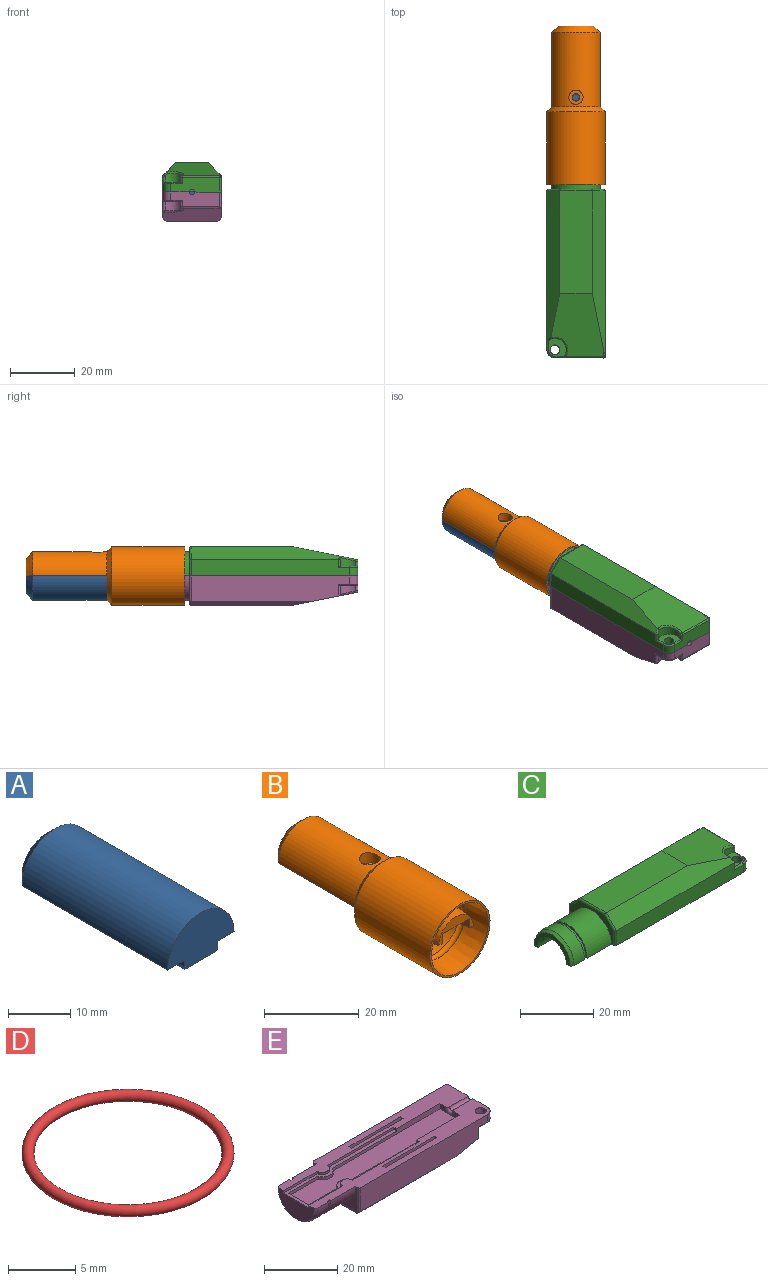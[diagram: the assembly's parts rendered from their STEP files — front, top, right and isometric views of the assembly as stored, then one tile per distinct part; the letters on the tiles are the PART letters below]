
ASSEMBLY  parts=5 mates=4
PART A: 19 faces, bbox 15x35x9.3 mm
  f0: plane 11x5.5mm, normal (0,1,0), area 43mm2, adj f1,f4,f13
  f1: plane 35x15mm, normal (0,0,-1), area 426.5mm2, adj f0,f2,f3,f4,f5,f6,f7,f8
  f2: cylinder r=7.5mm len=33mm, axis (0,1,0), area 777.5mm2, adj f1,f3,f13
  f3: plane 15x9.3mm, normal (0,-1,0), area 101.9mm2, adj f1,f2,f5,f6,f12,f17,f18
  f4: cylinder r=1.7mm len=17mm, axis (0,1,0), area 85mm2, adj f0,f1,f14
  f5: plane 11x1.2mm, normal (1,0,0), area 13.2mm2, adj f1,f3,f11,f18
  f6: plane 11x1.2mm, normal (-1,0,0), area 13.2mm2, adj f1,f3,f7,f17
  f7: plane 1.8x1mm, normal (0,1,0), area 1.7mm2, adj f1,f6,f8,f12,f17
  f8: plane 9x1.8mm, normal (1,0,0), area 16.2mm2, adj f1,f7,f9,f12
  f9: plane 5.6x1.8mm, normal (0,1,0), area 10.1mm2, adj f1,f8,f10,f12
  f10: plane 9x1.8mm, normal (-1,0,0), area 16.2mm2, adj f1,f9,f11,f12
  f11: plane 1.8x1mm, normal (0,1,0), area 1.7mm2, adj f1,f5,f10,f12,f18
  f12: plane 11x7.2mm, normal (0,0,-1), area 28.8mm2, adj f3,f7,f8,f9,f10,f11,f17,f18
  f13: cone r=7.5mm half-angle=45deg, axis (0,-1,0), area 57.8mm2, adj f0,f1,f2
  f14: plane 3.4x1.7mm, normal (0,0.71,-0.71), area 6.4mm2, adj f1,f4
  f15: cylinder r=1.05mm len=6mm, axis (0,0,-1), area 39.6mm2, adj f1,f16
  f16: plane 2.1x2.1mm, normal (0,0,-1), area 3.5mm2, adj f15
  f17: plane 11x0.6mm, normal (-0.95,0,-0.32), area 7mm2, adj f3,f6,f7,f12
  f18: plane 11x0.6mm, normal (0.95,0,-0.32), area 7mm2, adj f3,f5,f11,f12
PART B: 29 faces, bbox 18x48.9x18 mm
  f0: plane 15.6x15.6mm, normal (0,-1,0), area 52.9mm2, adj f4,f7,f8,f21,f28
  f1: cone r=9mm half-angle=45deg, axis (0,-1,0), area 106.6mm2, adj f3,f4,f7,f20,f28
  f2: cylinder r=1.7mm len=12.6mm, axis (0,1,0), area 66.5mm2, adj f4,f5,f7,f11,f25
  f3: cylinder r=7.5mm len=22.9mm, axis (0,1,0), area 524.2mm2, adj f1,f4,f7,f13,f15
  f4: plane 44.7x5.9mm, normal (0,0,-1), area 162.7mm2, adj f0,f1,f2,f3,f5,f8,f9,f11
  f5: plane 11x5.5mm, normal (0,1,0), area 43mm2, adj f2,f4,f7,f13
  f6: plane 10.38x4.9mm, normal (0,-1,0), area 20.2mm2, adj f9,f10,f12,f17,f18,f19
  f7: plane 44.7x5.9mm, normal (0,0,-1), area 162.7mm2, adj f0,f1,f2,f3,f5,f8,f10,f11
  f8: cylinder r=5.5mm len=11mm, axis (0,1,0), area 186.6mm2, adj f0,f4,f7,f17
  f9: plane 35.1x2.7mm, normal (-1,0,0), area 94.3mm2, adj f4,f6,f11,f12,f18
  f10: plane 35.1x2.7mm, normal (1,0,0), area 94.3mm2, adj f6,f7,f11,f12,f19
  f11: plane 8x2.7mm, normal (0,-1,0), area 17.1mm2, adj f2,f4,f7,f9,f10,f12
  f12: plane 35.1x8mm, normal (0,0,-1), area 276.6mm2, adj f6,f9,f10,f11,f14
  f13: cone r=7.5mm half-angle=45deg, axis (0,-1,0), area 57.8mm2, adj f3,f4,f5,f7
  f14: cylinder r=1.15mm len=2.3mm, axis (0,0,-1), area 14.5mm2, adj f12,f16
  f15: cylinder r=2.2mm len=4.4mm, axis (0,0,-1), area 36.4mm2, adj f3,f16
  f16: plane 4.4x4.4mm, normal (0,0,1), area 11.1mm2, adj f14,f15
  f17: cone r=5.2mm half-angle=5.7deg, axis (0,1,0), area 49.8mm2, adj f6,f8,f18,f19
  f18: plane 3.01x1.51mm, normal (0,-0.1,-1), area 4.1mm2, adj f4,f6,f9,f17
  f19: plane 3.01x1.51mm, normal (0,-0.1,-1), area 4.1mm2, adj f6,f7,f10,f17
  f20: cylinder r=9mm len=22.5mm, axis (0,-1,0), area 1272.3mm2, adj f1,f24
  f21: cylinder r=7.8mm len=15.6mm, axis (0,-1,0), area 358.8mm2, adj f0,f22
  f22: torus R=7.3mm, axis (0,-1,0), area 85.6mm2, adj f21,f23
  f23: cone r=8.5mm half-angle=5.2deg, axis (0,-1,0), area 322.7mm2, adj f22,f24
  f24: plane 18x18mm, normal (0,-1,0), area 27.5mm2, adj f20,f23
  f25: cylinder r=0.5mm len=1mm, axis (0,0,1), area 0.2mm2, adj f2,f27
  f26: plane 0.4x0.4mm, normal (0,0,-1), area 0.1mm2, adj f27
  f27: cone r=0.2mm half-angle=45deg, axis (0,0,1), area 0.9mm2, adj f25,f26
  f28: cylinder r=7.6mm len=15.2mm, axis (0,-1,0), area 212.5mm2, adj f0,f1,f4,f7
PART C: 64 faces, bbox 67.6x18.2x10 mm
  f0: plane 67.4x18mm, normal (0,0,-1), area 609.6mm2, adj f2,f3,f4,f6,f7,f9,f10,f11
  f1: plane 5.5x5.5mm, normal (0,0,1), area 18.9mm2, adj f53,f54,f56,f57,f59,f61,f63
  f2: plane 45.1x2.2mm, normal (0,-1,0), area 99.2mm2, adj f0,f17,f18,f52
  f3: cylinder r=7.5mm len=15mm, axis (1,0,0), area 221.5mm2, adj f0,f4,f31
  f4: plane 17x8.5mm, normal (-1,0,0), area 42.4mm2, adj f0,f3,f42,f43,f44,f45,f46
  f5: plane 31.5x10mm, normal (0,0,1), area 315mm2, adj f8,f12,f13,f44
  f6: plane 49x5mm, normal (0,-1,0), area 236.3mm2, adj f0,f13,f45,f55,f56,f57
  f7: plane 51x5mm, normal (0,1,0), area 254.6mm2, adj f0,f12,f42,f47,f49
  f8: plane 19.62x16.25mm, normal (0.2,0,0.98), area 246.1mm2, adj f5,f12,f13,f48,f49,f58,f60
  f9: plane 15x4.59mm, normal (1,0,0), area 60.3mm2, adj f0,f19,f47,f48,f55,f61,f63
  f10: cylinder r=7.5mm len=15mm, axis (1,0,0), area 94.2mm2, adj f0,f32,f51
  f11: plane 14x7mm, normal (-1,0,0), area 29.5mm2, adj f0,f14,f51
  f12: plane 50.02x4mm, normal (0,0.71,0.71), area 234.4mm2, adj f5,f7,f8,f43,f49
  f13: plane 45.62x4mm, normal (0,-0.71,0.71), area 229.4mm2, adj f5,f6,f8,f46,f56,f58
  f14: cylinder r=5.5mm len=12.8mm, axis (-1,0,0), area 221.2mm2, adj f0,f11,f15
  f15: plane 11x5.5mm, normal (-1,0,0), area 47.5mm2, adj f0,f14
  f16: plane 45.1x2.2mm, normal (0,1,0), area 99.2mm2, adj f0,f17,f18,f52
  f17: plane 45.1x8mm, normal (0,0,-1), area 360.8mm2, adj f2,f16,f18,f52
  f18: plane 8x2.2mm, normal (-1,0,0), area 13.1mm2, adj f0,f2,f16,f17,f41
  f19: cylinder r=0.9mm len=7.2mm, axis (-1,0,0), area 20.4mm2, adj f0,f9,f41
  f20: plane 0.8x0.8mm, normal (-1,0,0), area 0.6mm2, adj f0,f21,f23,f38
  f21: plane 19.4x0.8mm, normal (0,1,0), area 15.5mm2, adj f0,f20,f22,f37
  f22: plane 0.8x0.8mm, normal (1,0,0), area 0.6mm2, adj f0,f21,f23,f39
  f23: plane 19.4x0.8mm, normal (0,-1,0), area 15.5mm2, adj f0,f20,f22,f40
  f24: plane 19x0.4mm, normal (0,0,-1), area 7.6mm2, adj f37,f38,f39,f40
  f25: plane 0.8x0.8mm, normal (-1,0,0), area 0.6mm2, adj f0,f26,f28,f34
  f26: plane 19.4x0.8mm, normal (0,1,0), area 15.5mm2, adj f0,f25,f27,f33
  f27: plane 0.8x0.8mm, normal (1,0,0), area 0.6mm2, adj f0,f26,f28,f35
  f28: plane 19.4x0.8mm, normal (0,-1,0), area 15.5mm2, adj f0,f25,f27,f36
  f29: plane 19x0.4mm, normal (0,0,-1), area 7.6mm2, adj f33,f34,f35,f36
  f30: cylinder r=7mm len=14mm, axis (-1,0,0), area 22mm2, adj f0,f31,f32
  f31: plane 15x7.5mm, normal (-1,0,0), area 11.4mm2, adj f0,f3,f30
  f32: plane 15x7.5mm, normal (1,0,0), area 11.4mm2, adj f0,f10,f30
  f33: plane 19.4x0.2mm, normal (0,0.71,-0.71), area 5.4mm2, adj f26,f29,f34,f35
  f34: plane 0.8x0.2mm, normal (-0.71,0,-0.71), area 0.2mm2, adj f25,f29,f33,f36
  f35: plane 0.8x0.2mm, normal (0.71,0,-0.71), area 0.2mm2, adj f27,f29,f33,f36
  f36: plane 19.4x0.2mm, normal (0,-0.71,-0.71), area 5.4mm2, adj f28,f29,f34,f35
  f37: plane 19.4x0.2mm, normal (0,0.71,-0.71), area 5.4mm2, adj f21,f24,f38,f39
  f38: plane 0.8x0.2mm, normal (-0.71,0,-0.71), area 0.2mm2, adj f20,f24,f37,f40
  f39: plane 0.8x0.2mm, normal (0.71,0,-0.71), area 0.2mm2, adj f22,f24,f37,f40
  f40: plane 19.4x0.2mm, normal (0,-0.71,-0.71), area 5.4mm2, adj f23,f24,f38,f39
  f41: torus R=1.7mm, axis (-1,0,0), area 4.7mm2, adj f0,f18,f19
  f42: cylinder r=0.5mm len=5mm, axis (0,0,1), area 3.8mm2, adj f0,f4,f7,f43
  f43: cylinder r=0.5mm len=4.35mm, axis (0,-0.71,0.71), area 4.3mm2, adj f4,f12,f42,f44
  f44: cylinder r=0.5mm len=10mm, axis (0,1,0), area 7.7mm2, adj f4,f5,f43,f46
  f45: cylinder r=0.5mm len=5mm, axis (0,0,-1), area 3.8mm2, adj f0,f4,f6,f46
  f46: cylinder r=0.5mm len=4.35mm, axis (0,-0.71,-0.71), area 4.3mm2, adj f4,f13,f44,f45
  f47: cylinder r=0.5mm len=4.59mm, axis (0,0,-1), area 3.6mm2, adj f0,f7,f9,f50
  f48: cylinder r=0.5mm len=11.54mm, axis (0,1,0), area 7.9mm2, adj f8,f9,f50,f62
  f49: cylinder r=0.5mm len=2.2mm, axis (0.98,0,-0.2), area 1.1mm2, adj f7,f8,f12,f50
  f50: sphere r=0.5mm, area 0.5mm2, adj f47,f48,f49
  f51: cone r=7mm half-angle=26.6deg, axis (1,0,0), area 25.5mm2, adj f0,f10,f11
  f52: plane 8x2.2mm, normal (1,0,0), area 17.6mm2, adj f0,f2,f16,f17
  f53: cylinder r=3.5mm len=5.25mm, axis (0,0,1), area 20mm2, adj f1,f56,f58,f60,f63
  f54: cylinder r=1.5mm len=3mm, axis (0,0,1), area 28.3mm2, adj f0,f1
  f55: cylinder r=2.5mm len=2.5mm, axis (0,0,1), area 9.8mm2, adj f0,f6,f9,f59
  f56: cylinder r=0.5mm len=2.52mm, axis (0,0,1), area 2.2mm2, adj f1,f6,f13,f53,f57,f58
  f57: cylinder r=0.5mm len=3.46mm, axis (-1,0,0), area 2.5mm2, adj f1,f6,f56,f59
  f58: bspline ~1.75x1.64mm, area 1.5mm2, adj f8,f13,f53,f56,f60
  f59: torus R=2mm, axis (0,0,1), area 2.9mm2, adj f1,f55,f57,f61
  f60: bspline ~6x5.21mm, area 6.6mm2, adj f8,f53,f58,f62
  f61: cylinder r=0.5mm len=3.46mm, axis (0,-1,0), area 2.5mm2, adj f1,f9,f59,f63
  f62: sphere r=0.5mm, area 0.5mm2, adj f48,f60,f63
  f63: cylinder r=0.5mm len=2.09mm, axis (0,0,1), area 1.9mm2, adj f1,f9,f53,f61,f62
PART D: 1 faces, bbox 17.1x17.1x0.9 mm
  f0: torus R=7.45mm, axis (0,0,-1), area 130.8mm2
PART E: 65 faces, bbox 67.6x18.2x9 mm
  f0: plane 67.4x8.1mm, normal (0,0,1), area 280.3mm2, adj f1,f2,f5,f6,f8,f9,f13,f17
  f1: plane 49x8mm, normal (0,-1,0), area 364.8mm2, adj f0,f12,f14,f47,f57,f58,f59
  f2: plane 15x4.59mm, normal (1,0,0), area 60.3mm2, adj f0,f4,f50,f51,f53,f57,f63,f64
  f3: plane 5.5x5.5mm, normal (0,0,-1), area 18.9mm2, adj f55,f56,f58,f59,f61,f63,f64
  f4: plane 67.4x8.1mm, normal (0,0,1), area 288.7mm2, adj f2,f5,f6,f8,f9,f11,f13,f16
  f5: plane 7.6x1.8mm, normal (-1,0,0), area 9.1mm2, adj f0,f4,f21,f22,f31,f54
  f6: cylinder r=7.5mm len=15mm, axis (1,0,0), area 221.5mm2, adj f0,f4,f9,f43
  f7: plane 42.6x9.8mm, normal (0,0,1), area 101.8mm2, adj f8,f16,f17,f18,f19,f20,f21,f22
  f8: plane 14x7mm, normal (-1,0,0), area 69.1mm2, adj f0,f4,f7,f16,f17,f52
  f9: plane 17x8.5mm, normal (-1,0,0), area 55.6mm2, adj f0,f4,f6,f45,f46,f47,f48,f49
  f10: plane 31.5x16mm, normal (0,0,-1), area 504mm2, adj f12,f14,f15,f48
  f11: plane 51x8mm, normal (0,1,0), area 387mm2, adj f4,f12,f15,f45,f50
  f12: plane 19.6x18.01mm, normal (0.2,0,-0.98), area 319.4mm2, adj f1,f10,f11,f14,f15,f50,f51,f58
  f13: cylinder r=7.5mm len=15mm, axis (1,0,0), area 94.2mm2, adj f0,f4,f44,f52
  f14: plane 36.5x1mm, normal (0,-0.71,-0.71), area 48.1mm2, adj f1,f10,f12,f49
  f15: plane 36.5x1mm, normal (0,0.71,-0.71), area 48.1mm2, adj f10,f11,f12,f46
  f16: plane 13.05x0.8mm, normal (0,-1,0), area 10.4mm2, adj f4,f7,f8,f25
  f17: plane 13.05x0.8mm, normal (0,1,0), area 10.4mm2, adj f0,f7,f8,f18
  f18: cylinder r=1.95mm len=3.9mm, axis (0,0,1), area 4.9mm2, adj f0,f7,f17,f19
  f19: plane 25.65x0.8mm, normal (0,1,0), area 20.5mm2, adj f0,f7,f18,f20
  f20: plane 1.1x0.8mm, normal (-1,0,0), area 0.9mm2, adj f0,f7,f19,f21
  f21: plane 41.66x1.8mm, normal (0,1,0), area 55.1mm2, adj f0,f5,f7,f20,f30,f31
  f22: plane 41.66x1.8mm, normal (0,-1,0), area 55.1mm2, adj f4,f5,f7,f23,f26,f31
  f23: plane 1.1x0.8mm, normal (-1,0,0), area 0.9mm2, adj f4,f7,f22,f24
  f24: plane 25.65x0.8mm, normal (0,-1,0), area 20.5mm2, adj f4,f7,f23,f25
  f25: cylinder r=1.95mm len=3.9mm, axis (0,0,1), area 4.9mm2, adj f4,f7,f16,f24
  f26: cylinder r=2.95mm len=5.51mm, axis (0,0,1), area 7.1mm2, adj f7,f22,f27,f31
  f27: plane 11.22x1mm, normal (0,-1,0), area 11.2mm2, adj f7,f26,f28,f31
  f28: plane 7.8x1mm, normal (1,0,0), area 7.8mm2, adj f7,f27,f29,f31
  f29: plane 11.22x1mm, normal (0,1,0), area 11.2mm2, adj f7,f28,f30,f31
  f30: cylinder r=2.95mm len=5.51mm, axis (0,0,1), area 7.1mm2, adj f7,f21,f29,f31
  f31: plane 58.4x7.8mm, normal (0,0,1), area 431.4mm2, adj f5,f21,f22,f26,f27,f28,f29,f30
  f32: plane 20x1.2mm, normal (0,-1,0), area 24mm2, adj f0,f33,f35,f36
  f33: plane 1.2x1mm, normal (1,0,0), area 1.2mm2, adj f0,f32,f34,f36
  f34: plane 20x1.2mm, normal (0,1,0), area 24mm2, adj f0,f33,f35,f36
  f35: plane 1.2x1mm, normal (-1,0,0), area 1.2mm2, adj f0,f32,f34,f36
  f36: plane 20x1mm, normal (0,0,1), area 20mm2, adj f32,f33,f34,f35
  f37: plane 20x1.2mm, normal (0,-1,0), area 24mm2, adj f4,f38,f40,f41
  f38: plane 1.2x1mm, normal (1,0,0), area 1.2mm2, adj f4,f37,f39,f41
  f39: plane 20x1.2mm, normal (0,1,0), area 24mm2, adj f4,f38,f40,f41
  f40: plane 1.2x1mm, normal (-1,0,0), area 1.2mm2, adj f4,f37,f39,f41
  f41: plane 20x1mm, normal (0,0,1), area 20mm2, adj f37,f38,f39,f40
  f42: cylinder r=7mm len=14mm, axis (-1,0,0), area 22mm2, adj f0,f4,f43,f44
  f43: plane 15x7.5mm, normal (-1,0,0), area 11.4mm2, adj f0,f4,f6,f42
  f44: plane 15x7.5mm, normal (1,0,0), area 11.4mm2, adj f0,f4,f13,f42
  f45: cylinder r=0.5mm len=8mm, axis (0,0,1), area 6.2mm2, adj f4,f9,f11,f46
  f46: cylinder r=0.5mm len=1.35mm, axis (0,0.71,0.71), area 0.9mm2, adj f9,f15,f45,f48
  f47: cylinder r=0.5mm len=8mm, axis (0,0,-1), area 6.2mm2, adj f0,f1,f9,f49
  f48: cylinder r=0.5mm len=16mm, axis (0,-1,0), area 12.4mm2, adj f9,f10,f46,f49
  f49: cylinder r=0.5mm len=1.35mm, axis (0,0.71,-0.71), area 0.9mm2, adj f9,f14,f47,f48
  f50: cylinder r=0.5mm len=5.1mm, axis (0,0,-1), area 3.9mm2, adj f2,f4,f11,f12,f51
  f51: cylinder r=0.5mm len=12.03mm, axis (0,-1,0), area 8.1mm2, adj f2,f12,f50,f62
  f52: cone r=7mm half-angle=26.6deg, axis (1,0,0), area 25.5mm2, adj f0,f4,f8,f13
  f53: cylinder r=0.9mm len=7.2mm, axis (1,0,0), area 20.4mm2, adj f0,f2,f4,f54
  f54: torus R=1.7mm, axis (-1,0,0), area 4.7mm2, adj f0,f4,f5,f53
  f55: cylinder r=3.5mm len=5.25mm, axis (0,0,-1), area 19.6mm2, adj f3,f58,f60,f64
  f56: cylinder r=1.5mm len=3mm, axis (0,0,-1), area 28.3mm2, adj f0,f3
  f57: cylinder r=2.5mm len=2.5mm, axis (0,0,-1), area 9.8mm2, adj f0,f1,f2,f61
  f58: cylinder r=0.5mm len=3.69mm, axis (0,0,-1), area 3.3mm2, adj f1,f3,f12,f55,f59,f60
  f59: cylinder r=0.5mm len=3.46mm, axis (1,0,0), area 2.5mm2, adj f1,f3,f58,f61
  f60: bspline ~6.37x6mm, area 7.3mm2, adj f12,f55,f58,f62
  f61: torus R=2mm, axis (0,0,-1), area 2.9mm2, adj f3,f57,f59,f63
  f62: sphere r=0.5mm, area 0.5mm2, adj f51,f60,f64
  f63: cylinder r=0.5mm len=3.46mm, axis (0,1,0), area 2.5mm2, adj f2,f3,f61,f64
  f64: cylinder r=0.5mm len=2.09mm, axis (0,0,-1), area 1.9mm2, adj f2,f3,f55,f62,f63
PLACE A rot(axis=(0,-1,0),180deg) t=(-29.95,-76.52,6.27)mm
PLACE B t=(-29.95,-76.52,6.27)mm
PLACE C rot(axis=(0,0,-1),90deg) t=(-29.95,-152.92,-2.73)mm
PLACE D rot(axis=(-1,0,0),90deg) t=(-29.95,-117.02,6.27)mm
PLACE E rot(axis=(0,0,-1),90deg) t=(-29.95,-152.92,-2.73)mm fixed
MATE fastened E.f4 <-> C.f0  axis (0,0,-1) through (-20.95,-178.42,6.27)mm
MATE revolute C.f3 <-> D.f0  axis (0,1,0) through (-29.95,-117.02,6.27)mm
MATE cylindrical C.f3 <-> D.f0  axis (0,1,0) through (-29.95,-111.52,6.27)mm
MATE fastened A.f1 <-> B.f4  axis (0,0,-1) through (-28.25,-76.52,6.27)mm
